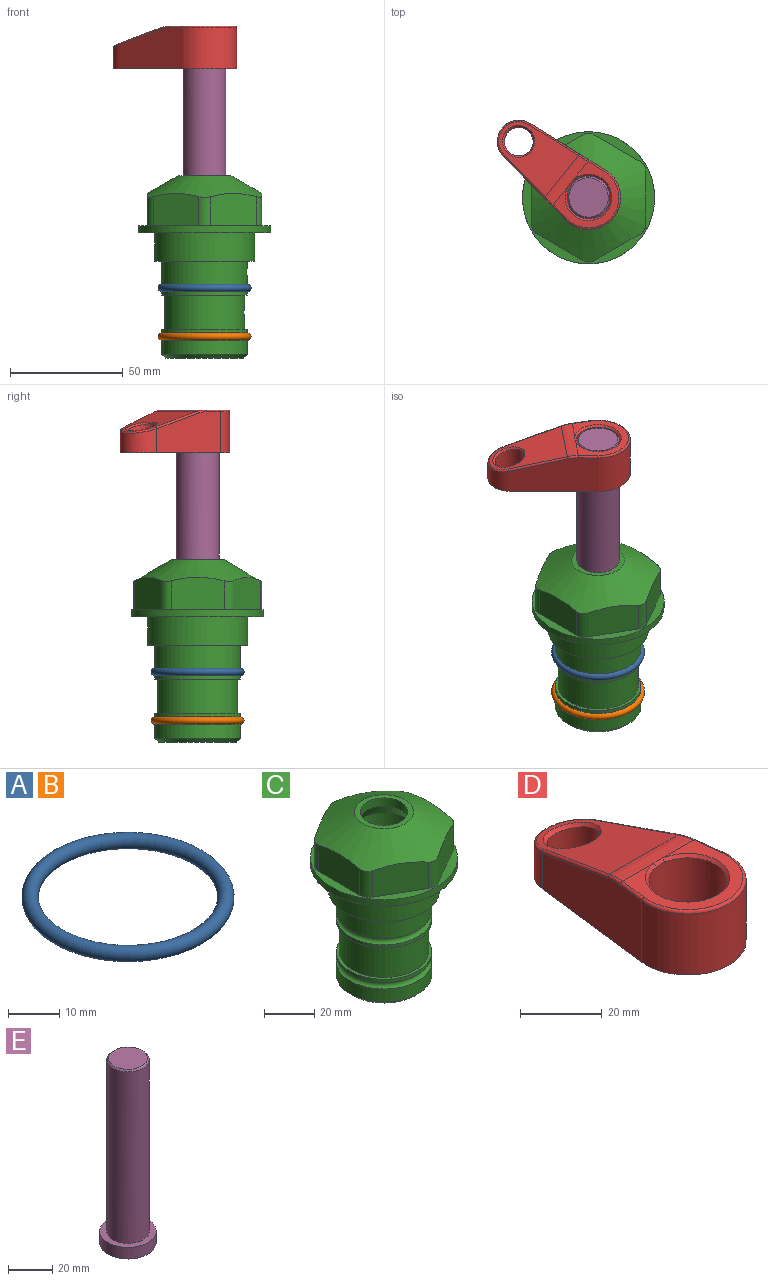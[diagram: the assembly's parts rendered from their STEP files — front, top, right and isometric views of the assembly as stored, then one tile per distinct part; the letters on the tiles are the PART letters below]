
ASSEMBLY  parts=5 mates=4
PART A: 1 faces, bbox 44.7x44.7x3.2 mm
  f0: torus R=19.05mm, axis (0,0,1), area 1193.9mm2
PART B: same geometry as A
PART C: 36 faces, bbox 58.7x58.7x81 mm
  f0: cylinder r=17.78mm len=35.56mm, axis (0,0,1), area 1670.8mm2, adj f23,f24,f31
  f1: cylinder r=19.05mm len=38.1mm, axis (0,0,1), area 1191.9mm2, adj f26,f27,f30
  f2: plane 58.66x58.66mm, normal (0,0,-1), area 1150.6mm2, adj f3,f28
  f3: cylinder r=29.33mm len=58.66mm, axis (0,0,-1), area 585.1mm2, adj f2,f4
  f4: plane 58.66x58.66mm, normal (0,0,1), area 475.9mm2, adj f3,f5,f6,f7,f8,f9,f10,f11
  f5: plane 20.32x14.34mm, normal (-0.5,0.87,0), area 324.4mm2, adj f4,f15,f16,f17
  f6: plane 20.32x14.34mm, normal (0.5,0.87,0), area 324.4mm2, adj f4,f14,f15,f17
  f7: plane 23.48x14.34mm, normal (1,0,0), area 324.4mm2, adj f4,f13,f14,f17
  f8: plane 20.32x14.34mm, normal (0.5,-0.87,0), area 324.4mm2, adj f4,f12,f13,f17
  f9: plane 20.32x14.34mm, normal (-0.5,-0.87,0), area 324.4mm2, adj f4,f11,f12,f17
  f10: plane 23.48x14.34mm, normal (-1,0,0), area 324.4mm2, adj f4,f11,f16,f17
  f11: cylinder r=5.08mm len=12.85mm, axis (0,0,-1), area 67.2mm2, adj f4,f9,f10,f17
  f12: cylinder r=5.08mm len=12.85mm, axis (0,0,-1), area 67.2mm2, adj f4,f8,f9,f17
  f13: cylinder r=5.08mm len=12.85mm, axis (0,0,-1), area 67.2mm2, adj f4,f7,f8,f17
  f14: cylinder r=5.08mm len=12.85mm, axis (0,0,-1), area 67.2mm2, adj f4,f6,f7,f17
  f15: cylinder r=5.08mm len=12.85mm, axis (0,0,-1), area 67.2mm2, adj f4,f5,f6,f17
  f16: cylinder r=5.08mm len=12.85mm, axis (0,0,-1), area 67.2mm2, adj f4,f5,f10,f17
  f17: cone r=11.73mm half-angle=60deg, axis (0,0,-1), area 2071.8mm2, adj f5,f6,f7,f8,f9,f10,f11,f12
  f18: plane 23.46x23.46mm, normal (0,0,1), area 147.4mm2, adj f17,f35
  f19: plane 34.93x34.93mm, normal (0,0,-1), area 958mm2, adj f29
  f20: cylinder r=19.05mm len=38.1mm, axis (0,0,1), area 760.1mm2, adj f21,f29
  f21: torus R=19.05mm, axis (0,0,1), area 565.3mm2, adj f20,f22
  f22: cylinder r=19.05mm len=38.1mm, axis (0,0,1), area 190mm2, adj f21,f23
  f23: plane 38.1x38.1mm, normal (0,0,1), area 146.9mm2, adj f0,f22
  f24: plane 38.1x38.1mm, normal (0,0,-1), area 146.9mm2, adj f0,f25
  f25: cylinder r=19.05mm len=38.1mm, axis (0,0,1), area 190mm2, adj f24,f26
  f26: torus R=19.05mm, axis (0,0,1), area 565.3mm2, adj f1,f25
  f27: plane 44.45x44.45mm, normal (0,0,-1), area 411.7mm2, adj f1,f28
  f28: cylinder r=22.23mm len=44.45mm, axis (0,0,1), area 1773.5mm2, adj f2,f27
  f29: cone r=19.05mm half-angle=45deg, axis (0,0,1), area 257.5mm2, adj f19,f20
  f30: cylinder r=3.17mm len=6.75mm, axis (-1,0,0), area 128mm2, adj f1,f33
  f31: cylinder r=3.17mm len=6.35mm, axis (-1,0,0), area 102.5mm2, adj f0,f33
  f32: plane 25.4x25.4mm, normal (0,0,1), area 506.7mm2, adj f33
  f33: cylinder r=12.7mm len=66.42mm, axis (0,0,-1), area 5236.2mm2, adj f30,f31,f32,f34
  f34: cone r=9.53mm half-angle=30deg, axis (0,0,-1), area 443.4mm2, adj f33,f35
  f35: cylinder r=9.53mm len=19.05mm, axis (0,0,-1), area 240.9mm2, adj f18,f34
PART D: 31 faces, bbox 31.7x65.5x19.8 mm
  f0: plane 39.12x18.26mm, normal (0.99,0.12,0), area 612.2mm2, adj f1,f4,f7,f11,f13,f15
  f1: cylinder r=9.53mm len=18.91mm, axis (0,0,-1), area 296.1mm2, adj f0,f2,f7,f17
  f2: plane 39.12x18.26mm, normal (-0.99,0.12,0), area 612.2mm2, adj f1,f4,f7,f12,f14,f16
  f3: cylinder r=6.35mm len=12.7mm, axis (0,0,-1), area 362.4mm2, adj f7,f18
  f4: cylinder r=14.29mm len=28.58mm, axis (0,0,-1), area 882.2mm2, adj f0,f2,f7,f10
  f5: cylinder r=9.53mm len=19.05mm, axis (0,0,-1), area 1092.6mm2, adj f7,f19,f20
  f6: plane 26.99x23.69mm, normal (0,0,1), area 216.2mm2, adj f9,f10,f11,f12,f19
  f7: plane 63.5x28.58mm, normal (0,0,-1), area 661.8mm2, adj f0,f1,f2,f3,f4,f5,f22,f23
  f8: plane 33.52x23.6mm, normal (0,0.26,0.97), area 486mm2, adj f9,f15,f16,f17,f18
  f9: cylinder r=19.05mm len=24.72mm, axis (1,0,0), area 120.4mm2, adj f6,f8,f13,f14,f20
  f10: torus R=13.49mm, axis (0,0,1), area 59mm2, adj f4,f6,f11,f12
  f11: cylinder r=0.79mm len=8.67mm, axis (0.12,-0.99,0), area 10.8mm2, adj f0,f6,f10,f13
  f12: cylinder r=0.79mm len=8.67mm, axis (0.12,0.99,0), area 10.8mm2, adj f2,f6,f10,f14
  f13: bspline ~4.95x1.42mm, area 6.1mm2, adj f0,f9,f11,f15
  f14: bspline ~4.95x1.42mm, area 6.1mm2, adj f2,f9,f12,f16
  f15: cylinder r=0.79mm len=25.95mm, axis (0.12,-0.96,0.26), area 32.9mm2, adj f0,f8,f13,f17
  f16: cylinder r=0.79mm len=25.95mm, axis (0.12,0.96,-0.26), area 32.9mm2, adj f2,f8,f14,f17
  f17: bspline ~18.91x8.38mm, area 30mm2, adj f1,f8,f15,f16
  f18: bspline ~14.29x14.29mm, area 48.3mm2, adj f3,f8
  f19: cone r=9.53mm half-angle=45deg, axis (0,0,1), area 66.5mm2, adj f5,f6,f20
  f20: bspline ~3.22x0.96mm, area 3.5mm2, adj f5,f9,f19
  f21: plane 2.75x2.72mm, normal (0,0,-1), area 2.9mm2, adj f23,f25,f28
  f22: plane 23.05x15.88mm, normal (-0.99,-0.12,0), area 323.6mm2, adj f7,f25,f26,f27,f28,f29
  f23: plane 23.05x15.88mm, normal (0.99,-0.12,0), area 323.6mm2, adj f7,f21,f25,f27,f28,f30
  f24: cylinder r=9.53mm len=10.69mm, axis (0,0,-1), area 114.7mm2, adj f7,f27,f29,f30
  f25: cylinder r=12.7mm len=20.59mm, axis (0,0,-1), area 381.1mm2, adj f7,f21,f22,f23,f26,f28
  f26: plane 2.75x2.72mm, normal (0,0,-1), area 2.9mm2, adj f22,f25,f28
  f27: plane 19.72x18.37mm, normal (0,-0.26,-0.97), area 291.8mm2, adj f22,f23,f24,f28,f29,f30
  f28: cylinder r=15.88mm len=19.92mm, axis (1,0,0), area 54.8mm2, adj f21,f22,f23,f25,f26,f27
  f29: cylinder r=1.59mm len=11mm, axis (0,0,-1), area 34.7mm2, adj f7,f22,f24,f27
  f30: cylinder r=1.59mm len=11mm, axis (0,0,-1), area 34.7mm2, adj f7,f23,f24,f27
PART E: 6 faces, bbox 25.4x25.4x101.6 mm
  f0: plane 17.46x17.46mm, normal (0,0,1), area 239.5mm2, adj f5
  f1: plane 25.4x25.4mm, normal (0,0,-1), area 506.7mm2, adj f2
  f2: cylinder r=12.7mm len=25.4mm, axis (0,0,1), area 506.7mm2, adj f1,f3
  f3: plane 25.4x25.4mm, normal (0,0,1), area 221.7mm2, adj f2,f4
  f4: cylinder r=9.53mm len=94.46mm, axis (0,0,1), area 5653mm2, adj f3,f5
  f5: cone r=8.73mm half-angle=45deg, axis (0,0,-1), area 64.4mm2, adj f0,f4
PLACE A at identity
PLACE B t=(0,0,-21.59)mm
PLACE C at identity fixed
PLACE D rot(axis=(0,0,1),51.3deg) t=(0,0,28.35)mm
PLACE E rot(axis=(0,0,1),51.3deg) t=(0,0,27.55)mm
MATE cylindrical E.f2 <-> C.f0  axis (0,0,-1) through (0,0,-10.55)mm
MATE fastened A.f0 <-> C.f0  axis (0,0,1) through (0,0,-24.51)mm
MATE fastened B.f0 <-> C.f0  axis (0,0,1) through (0,0,-46.1)mm
MATE fastened D.f4 <-> E.f2  axis (0,0,-1) through (0,0,91.05)mm
